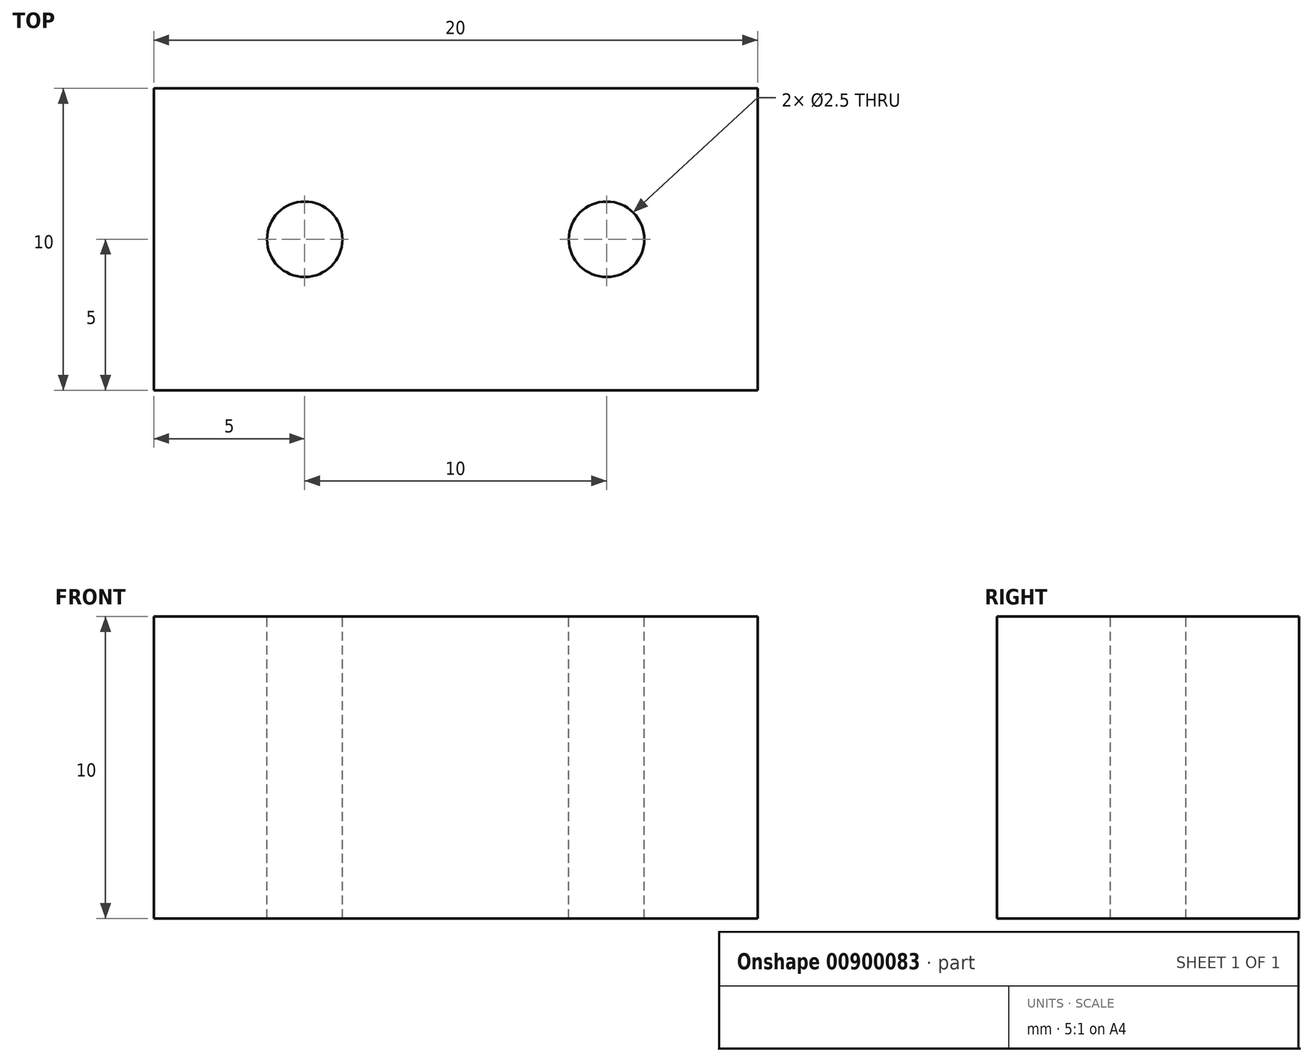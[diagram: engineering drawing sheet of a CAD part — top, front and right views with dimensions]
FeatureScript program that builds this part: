
annotation { "Feature Type Name" : "Feature", "Feature Type Description" : "" }
export const myFeature = defineFeature(function(context is Context, id is Id, definition is map)
    precondition{}
    {
        {
            var Q0;
            Q0=qCreatedBy(makeId("Top.planeOp"),FACE);
            var sketch = newSketch(context, id + "F0", { "sketchPlane" : qUnion([Q0])});
            skLineSegment(sketch, "E0.bottom", {"start": v(10, 5) * mm, "end": v(-10, 5) * mm});
            skLineSegment(sketch, "E0.top", {"start": v(10, -5) * mm, "end": v(-10, -5) * mm});
            skLineSegment(sketch, "E0.left", {"start": v(10, 5) * mm, "end": v(10, -5) * mm});
            skLineSegment(sketch, "E0.right", {"start": v(-10, 5) * mm, "end": v(-10, -5) * mm});
            skPoint(sketch, "E0.middle", {"position": v(0, 0) * mm});
            skLineSegment(sketch, "E1", {"start": v(-5, 0) * mm, "end": v(5, 0) * mm, "construction": true});
            skPoint(sketch, "E1.startSnap0", {"position": v(-10, 0) * mm});
            skSolve(sketch);
        }
        {
            var Q0;
            Q0=makeQuery(id+"F0.imprint","IMPRINT",FACE,{"disambiguationData":[TD([[makeQuery(id+"F0.imprint","IMPRINT",EDGE,{"derivedFrom":sQuery(id+"F0.wireOp",EDGE,"E0.bottom")}),1.0]])]});
            extrude(context, id + "F1", {"entities" : qUnion([Q0]), "oppositeDirection" : true, "depth" : 10 * mm, "offsetDistance" : 25 * mm});
        }
        {
            var Q0;
            Q0=sQuery(id+"F0.wireOp",VERTEX,"E1.start");
            var Q1;
            Q1=sQuery(id+"F0.wireOp",VERTEX,"E1.end");
            var Q2;
            Q2=makeQuery(id+"F1.opExtrude","SWEPT_BODY",BODY,{"disambiguationData":[OSD([sQuery(id+"F0.wireOp",EDGE,"E0.bottom"),sQuery(id+"F0.wireOp",EDGE,"E0.top"),sQuery(id+"F0.wireOp",EDGE,"E0.left"),sQuery(id+"F0.wireOp",EDGE,"E0.right")])]});
            hole(context, id + "F2", {"style" : HoleStyle.SIMPLE, "endStyle" : HoleEndStyle.THROUGH, "standardTappedOrClearance" : lookupTablePath({ "standard" : "ISO", "engagement" : "75%", "pitch" : "0.5 mm", "size" : "M3", "type" : "Tapped" }), "standardBlindInLast" : lookupTablePath({ "standard" : "ISO", "engagement" : "75%", "pitch" : "0.5 mm", "size" : "M3", "type" : "Tapped" }), "holeDiameter" : 2.5 * mm, "majorDiameter" : 3 * mm, "showTappedDepth" : true, "tappedDepth" : 12 * mm, "tapClearance" : 3, "startFromSketch" : true, "locations" : qUnion([Q0, Q1]), "scope" : qUnion([Q2])});
        }
    });
